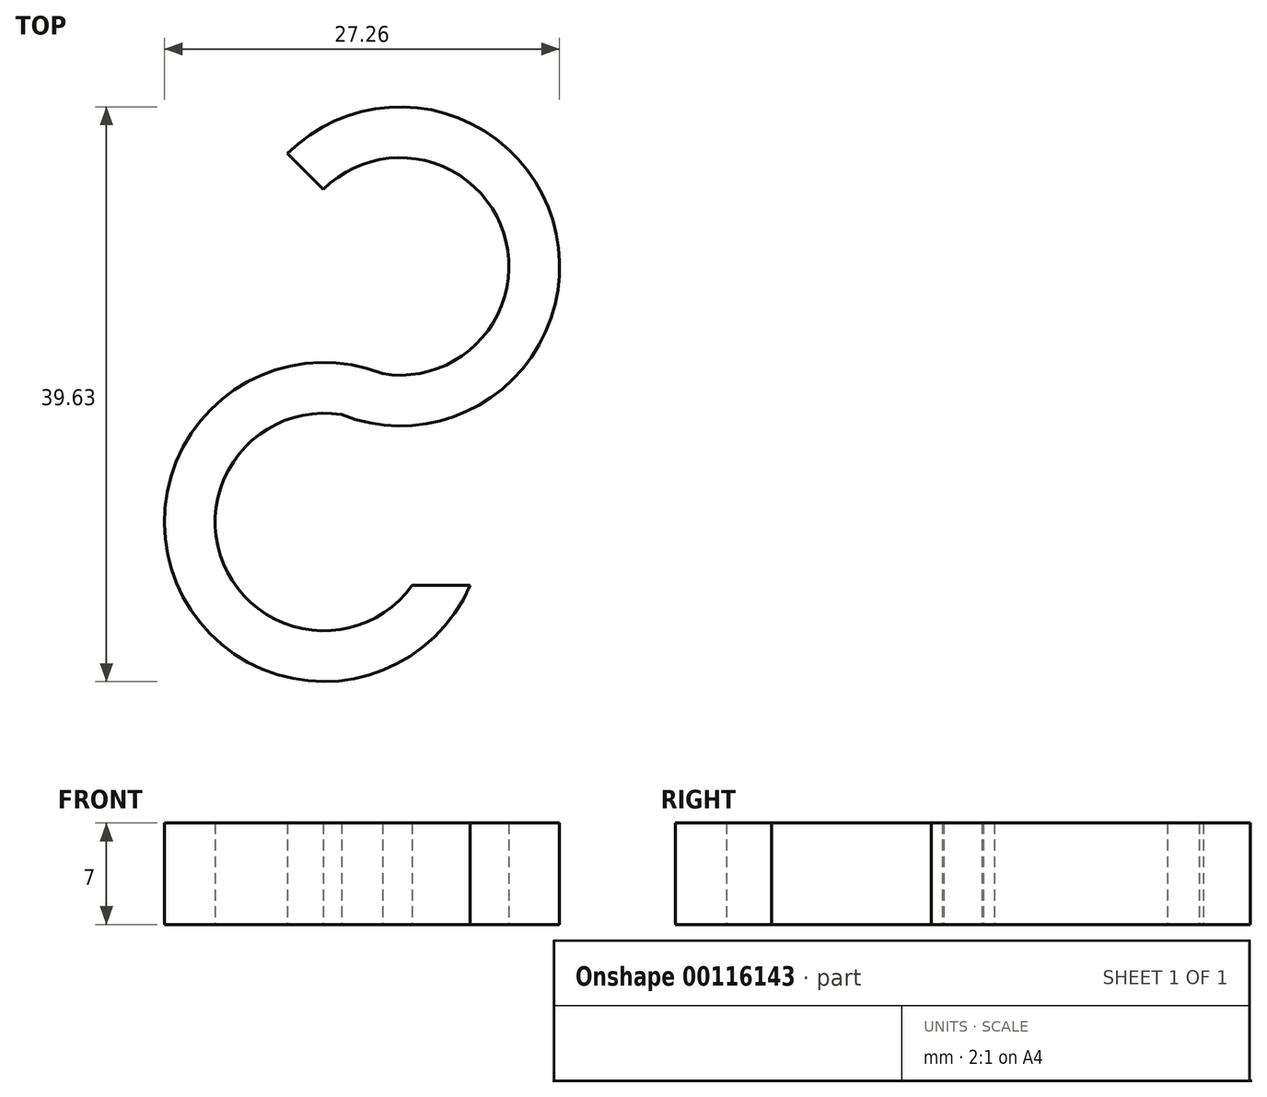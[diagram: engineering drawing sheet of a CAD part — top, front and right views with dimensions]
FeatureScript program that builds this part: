
annotation { "Feature Type Name" : "Feature", "Feature Type Description" : "" }
export const myFeature = defineFeature(function(context is Context, id is Id, definition is map)
    precondition{}
    {
        {
            var Q0;
            Q0=qCreatedBy(makeId("Top.planeOp"),FACE);
            var sketch = newSketch(context, id + "F0", { "sketchPlane" : qUnion([Q0])});
            skArc(sketch, "E0", {"start": v(-29.05, 14.77) * mm, "mid": v(-14.23, 27.23) * mm, "end": v(-32.78, 32.78) * mm});
            skLineSegment(sketch, "E1", {"start": v(-32.78, 32.78) * mm, "end": v(-30.3, 30.3) * mm});
            skArc(sketch, "E2", {"start": v(-26.22, 17.6) * mm, "mid": v(-17.86, 27.3) * mm, "end": v(-30.3, 30.3) * mm});
            skArc(sketch, "E3", {"start": v(-26.22, 17.6) * mm, "mid": v(-40.43, 3.16) * mm, "end": v(-20.17, 3) * mm});
            skArc(sketch, "E4", {"start": v(-29.05, 14.77) * mm, "mid": v(-37.2, 4.5) * mm, "end": v(-24.17, 3) * mm});
            skLineSegment(sketch, "E5", {"start": v(-24.17, 3) * mm, "end": v(-20.17, 3) * mm});
            skLineSegment(sketch, "E6", {"start": v(-29.05, 14.77) * mm, "end": v(-26.22, 17.6) * mm, "construction": true});
            skSolve(sketch);
        }
        {
            var Q0;
            Q0=makeQuery(id+"F0.imprint","IMPRINT",FACE,{"disambiguationData":[TD([[makeQuery(id+"F0.imprint","IMPRINT",EDGE,{"derivedFrom":sQuery(id+"F0.wireOp",EDGE,"E0")}),1.0]])]});
            extrude(context, id + "F1", {"entities" : qUnion([Q0]), "depth" : 7 * mm});
        }
    });
